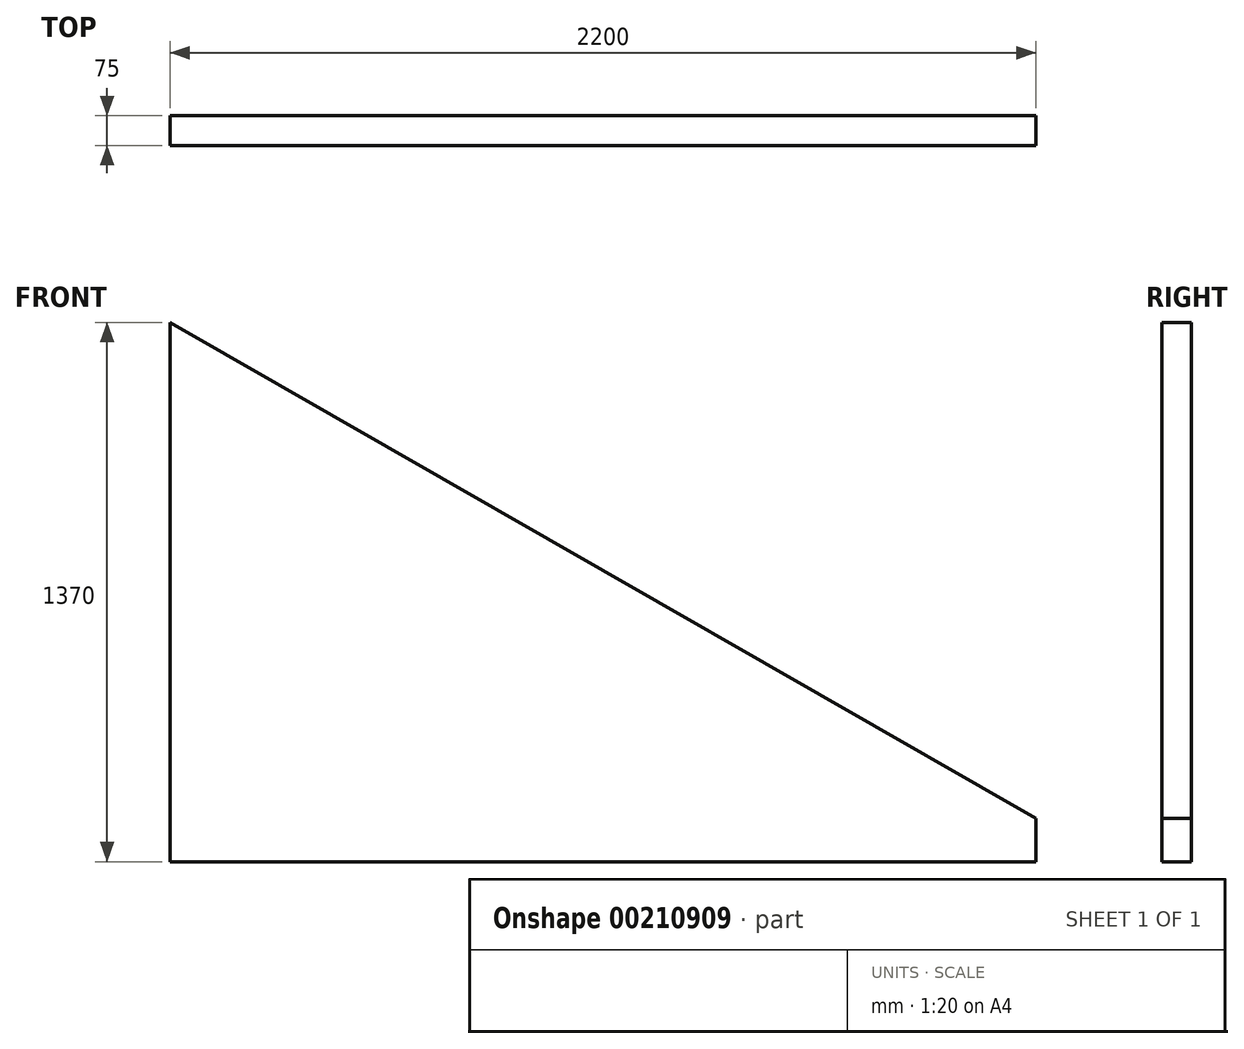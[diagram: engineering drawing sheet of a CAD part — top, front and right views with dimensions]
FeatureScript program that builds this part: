
annotation { "Feature Type Name" : "Feature", "Feature Type Description" : "" }
export const myFeature = defineFeature(function(context is Context, id is Id, definition is map)
    precondition{}
    {
        {
            var Q0;
            Q0=qCreatedBy(makeId("Front.planeOp"),FACE);
            var sketch = newSketch(context, id + "F0", { "sketchPlane" : qUnion([Q0])});
            skLineSegment(sketch, "E0.bottom", {"start": v(0, 0) * mm, "end": v(2200, 0) * mm});
            skLineSegment(sketch, "E0.right", {"start": v(2200, 0) * mm, "end": v(2200, 110) * mm});
            skLineSegment(sketch, "E1", {"start": v(0, 1370) * mm, "end": v(2200, 110) * mm});
            skLineSegment(sketch, "E2", {"start": v(0, 0) * mm, "end": v(0, 1370) * mm});
            skSolve(sketch);
        }
        {
            var Q0;
            Q0=makeQuery(id+"F0.imprint","IMPRINT",FACE,{"disambiguationData":[TD([[makeQuery(id+"F0.imprint","IMPRINT",EDGE,{"derivedFrom":sQuery(id+"F0.wireOp",EDGE,"E0.bottom")}),1.0]])]});
            extrude(context, id + "F1", {"entities" : qUnion([Q0]), "depth" : 75 * mm});
        }
    });
